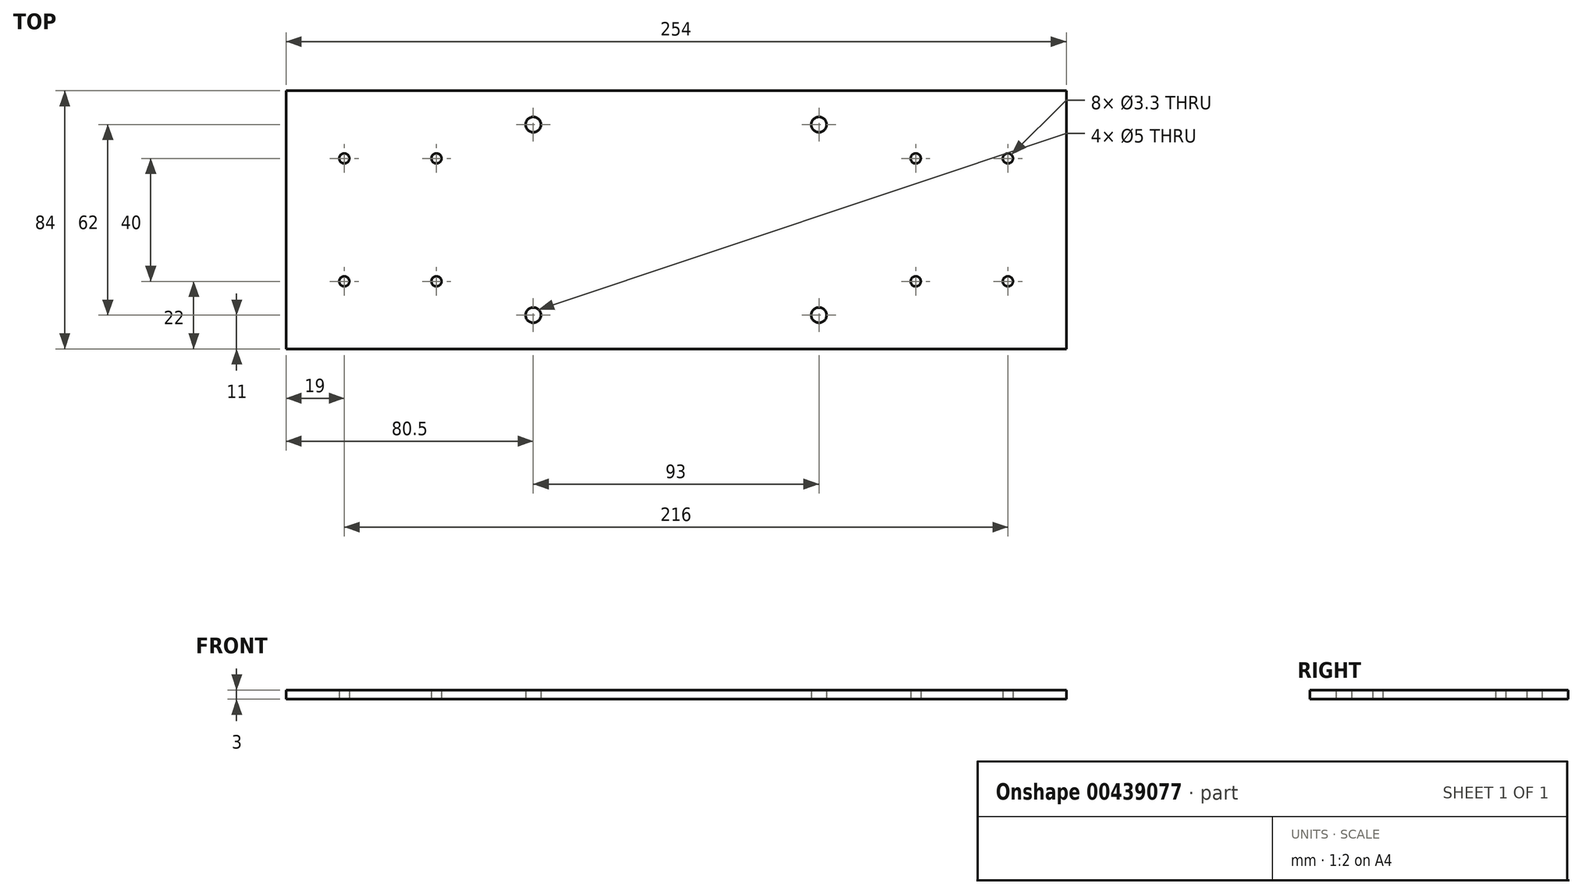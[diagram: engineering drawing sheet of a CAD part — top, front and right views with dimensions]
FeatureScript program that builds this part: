
annotation { "Feature Type Name" : "Feature", "Feature Type Description" : "" }
export const myFeature = defineFeature(function(context is Context, id is Id, definition is map)
    precondition{}
    {
        {
            var Q0;
            Q0=qCreatedBy(makeId("Top.planeOp"),FACE);
            var sketch = newSketch(context, id + "F0", { "sketchPlane" : qUnion([Q0])});
            skLineSegment(sketch, "E0.bottom", {"start": v(0, -84) * mm, "end": v(254, -84) * mm});
            skLineSegment(sketch, "E0.top", {"start": v(0, 0) * mm, "end": v(254, 0) * mm});
            skLineSegment(sketch, "E0.left", {"start": v(0, -84) * mm, "end": v(0, 0) * mm});
            skLineSegment(sketch, "E0.right", {"start": v(254, -84) * mm, "end": v(254, 0) * mm});
            skCircle(sketch, "E1", {"center": v(19, -22) * mm, "radius": 1.65 * mm});
            skCircle(sketch, "E2.0.1.0", {"center": v(19, -62) * mm, "radius": 1.65 * mm});
            skCircle(sketch, "E2.1.0.0", {"center": v(49, -22) * mm, "radius": 1.65 * mm});
            skCircle(sketch, "E2.1.1.0", {"center": v(49, -62) * mm, "radius": 1.65 * mm});
            skLineSegment(sketch, "E2.direction1", {"start": v(19, -22) * mm, "end": v(49, -22) * mm, "construction": true});
            skLineSegment(sketch, "E2.direction2", {"start": v(19, -22) * mm, "end": v(19, -62) * mm, "construction": true});
            skLineSegment(sketch, "E3.1.0.0", {"start": v(205, -22) * mm, "end": v(235, -22) * mm, "construction": true});
            skLineSegment(sketch, "E3.1.0.1", {"start": v(205, -22) * mm, "end": v(205, -62) * mm, "construction": true});
            skCircle(sketch, "E3.1.0.2", {"center": v(235, -62) * mm, "radius": 1.65 * mm});
            skCircle(sketch, "E3.1.0.3", {"center": v(235, -22) * mm, "radius": 1.65 * mm});
            skCircle(sketch, "E3.1.0.4", {"center": v(205, -62) * mm, "radius": 1.65 * mm});
            skCircle(sketch, "E3.1.0.5", {"center": v(205, -22) * mm, "radius": 1.65 * mm});
            skLineSegment(sketch, "E3.direction1", {"start": v(19, -62) * mm, "end": v(205, -62) * mm, "construction": true});
            skCircle(sketch, "E4", {"center": v(80.5, -11) * mm, "radius": 2.5 * mm});
            skCircle(sketch, "E5.0.1.0", {"center": v(80.5, -73) * mm, "radius": 2.5 * mm});
            skCircle(sketch, "E5.1.0.0", {"center": v(173.5, -11) * mm, "radius": 2.5 * mm});
            skCircle(sketch, "E5.1.1.0", {"center": v(173.5, -73) * mm, "radius": 2.5 * mm});
            skLineSegment(sketch, "E5.direction1", {"start": v(80.5, -11) * mm, "end": v(173.5, -11) * mm, "construction": true});
            skLineSegment(sketch, "E5.direction2", {"start": v(80.5, -11) * mm, "end": v(80.5, -73) * mm, "construction": true});
            skSolve(sketch);
        }
        {
            var Q0;
            Q0=makeQuery(id+"F0.imprint","IMPRINT",FACE,{"disambiguationData":[TD([[makeQuery(id+"F0.imprint","IMPRINT",EDGE,{"derivedFrom":sQuery(id+"F0.wireOp",EDGE,"E0.bottom")}),1.0]])]});
            extrude(context, id + "F1", {"entities" : qUnion([Q0]), "depth" : 3 * mm});
        }
    });
